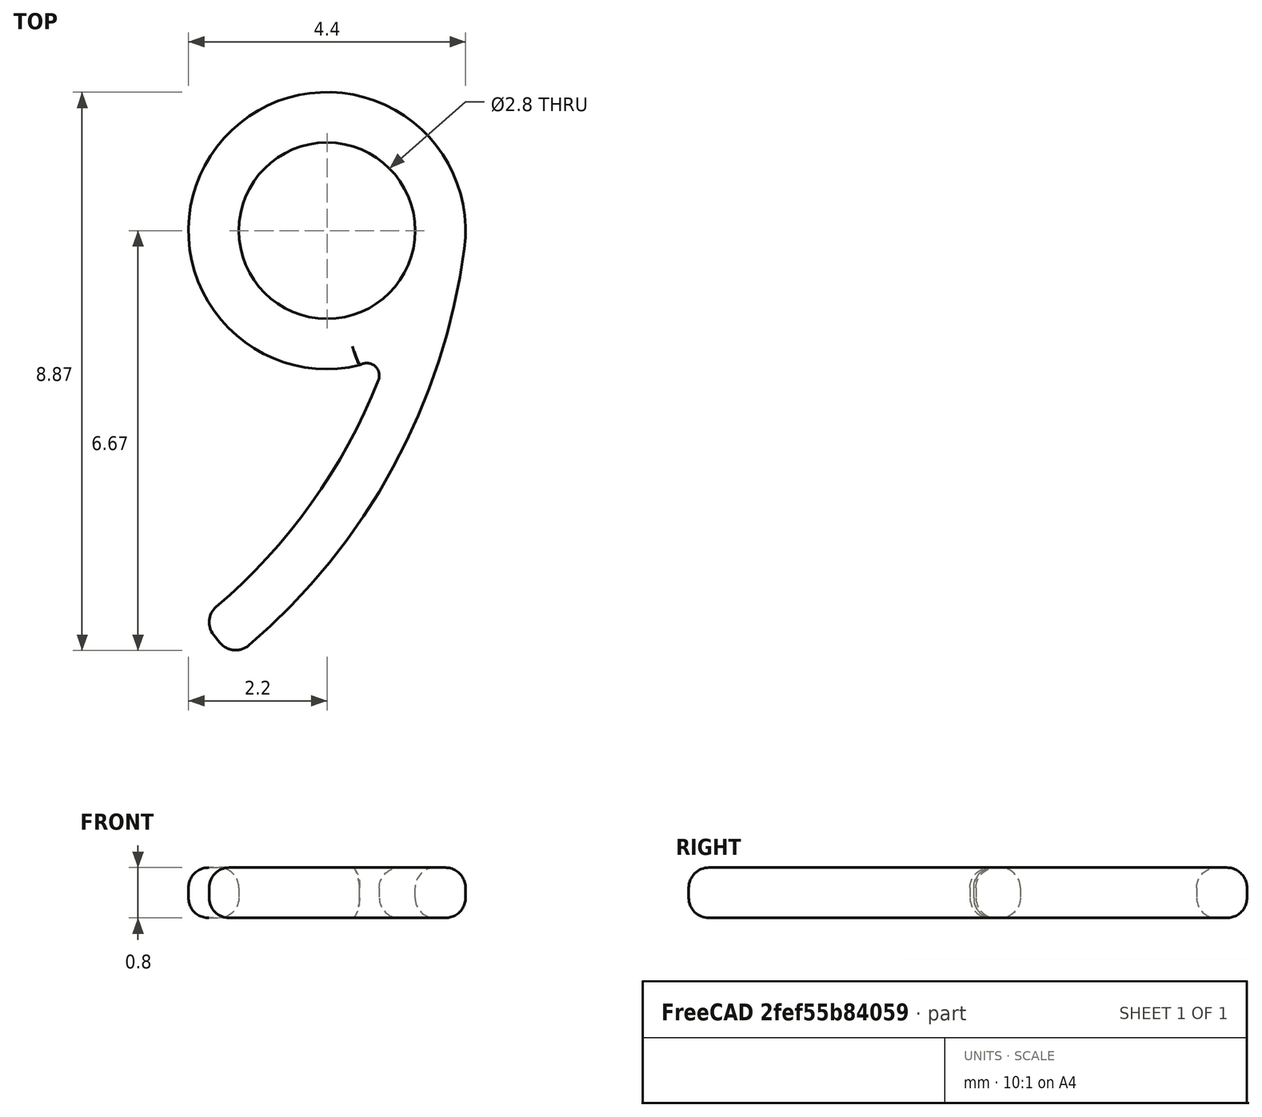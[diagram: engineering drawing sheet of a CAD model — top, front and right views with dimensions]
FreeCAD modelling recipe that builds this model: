
FCSTD DOCUMENT  (FreeCAD 0.16R6712 (Git))
Label: 9f
License: All rights reserved
LicenseURL: http://en.wikipedia.org/wiki/All_rights_reserved
objects: Sketcher::SketchObject×1, PartDesign::Pad×1, PartDesign::Fillet×1, Mesh::Feature×1
note: 4 computed .brp shape members not serialized (recipe doc carries the construction recipe); baked Part::Feature solids carry a one-line shape summary decoded from their .brp

FEATURE [Sketcher::SketchObject] Sketch
  sketch-geometry (6):
    g0: ArcOfCircle CenterX=-7.73305 CenterY=7.81979 CenterZ=0 NormalX=0 NormalY=0 NormalZ=1 Radius=10 StartAngle=5.38535 EndAngle=6.15207
    g1: ArcOfCircle CenterX=-7.73305 CenterY=7.81979 CenterZ=0 NormalX=0 NormalY=0 NormalZ=1 Radius=9.2 StartAngle=5.38535 EndAngle=5.90494
    g2: LineSegment StartX=-1.99864 StartY=0.625583 StartZ=0 EndX=-1.5 EndY=0 EndZ=0
    g3: ArcOfCircle CenterX=0.63079 CenterY=4.4962 CenterZ=0 NormalX=0 NormalY=0 NormalZ=1 Radius=0.2 StartAngle=5.90496 EndAngle=8.44641
    g4: ArcOfCircle CenterX=0 CenterY=6.8 CenterZ=0 NormalX=0 NormalY=0 NormalZ=1 Radius=2.2 StartAngle=6.15207 EndAngle=11.2338
    g5: Circle CenterX=0 CenterY=6.8 CenterZ=0 NormalX=0 NormalY=0 NormalZ=1 Radius=1.4
  constraints (20):
    c: PointOnObject(g0,g-1)
    c: Radius(g0) = 10
    c: Coincident(g1,g0)
    c: Radius(g1) = 9.2
    c: Coincident(g2,g0)
    c: PointOnObject(g1,g2)
    c: Perpendicular(g1,g2,g1) = 4.71239
    c: Coincident(g1,g2)
    c: DistanceX(g-2,g0) = -1.5
    c: PointOnObject(g3,g1)
    c: Tangent(g3,g1)
    c: Coincident(g3,g1)
    c: PointOnObject(g4,g-2)
    c: Coincident(g4,g3)
    c: Coincident(g4,g0)
    c: Radius(g4) = 2.2
    c: Coincident(g5,g4)
    c: Radius(g5) = 1.4
    c: DistanceY(g-1,g4) = 6.8
    c: Radius(g3) = 0.2
FEATURE [PartDesign::Pad] Pad
  Length = 0.8
  Length2 = 100
  Midplane = true
  Sketch = -> Sketch
  Type = 0
FEATURE [PartDesign::Fillet] Fillet
  Base = -> Pad [Edge4,Edge7,Edge10,Edge13,Edge15,Edge18,Edge1,Edge2,Edge3,Edge6,Edge9,Edge12,Edge14,Edge17]
  Radius = 0.32
FEATURE [Mesh::Feature] Mesh  label="Fillet (Meshed)"
